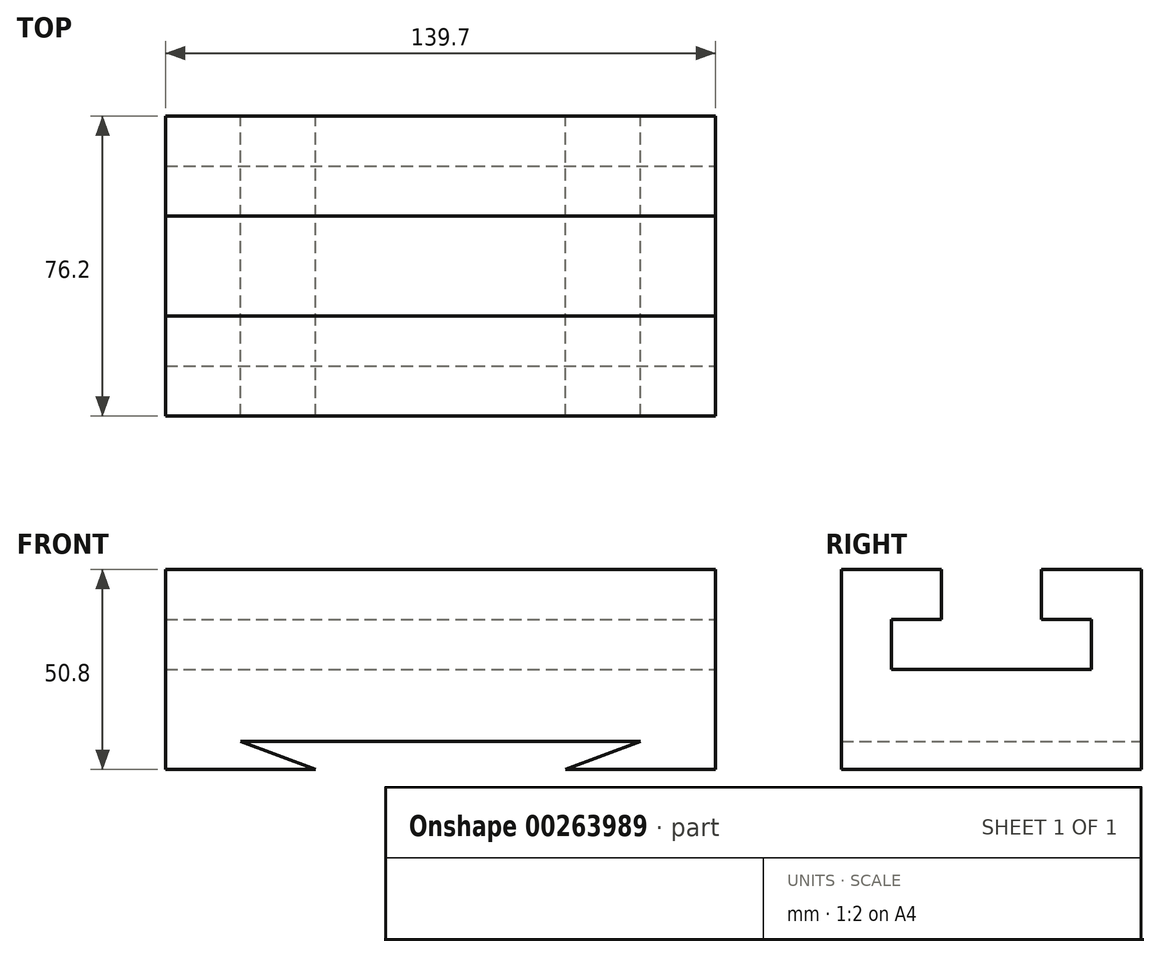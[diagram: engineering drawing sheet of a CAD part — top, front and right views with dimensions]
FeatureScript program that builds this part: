
annotation { "Feature Type Name" : "Feature", "Feature Type Description" : "" }
export const myFeature = defineFeature(function(context is Context, id is Id, definition is map)
    precondition{}
    {
        {
            var Q0;
            Q0=qCreatedBy(makeId("Front.planeOp"),FACE);
            var sketch = newSketch(context, id + "F0", { "sketchPlane" : qUnion([Q0])});
            skLineSegment(sketch, "E0", {"start": v(-77.12, 0) * mm, "end": v(-39.02, 0) * mm});
            skLineSegment(sketch, "E1", {"start": v(-39.02, 0) * mm, "end": v(-58.07, 7.07) * mm});
            skPoint(sketch, "E1.endSnap0", {"position": v(-58.07, 0) * mm});
            skLineSegment(sketch, "E2", {"start": v(-58.07, 7.07) * mm, "end": v(43.53, 7.07) * mm});
            skLineSegment(sketch, "E3", {"start": v(43.53, 7.07) * mm, "end": v(24.48, 0) * mm});
            skLineSegment(sketch, "E4", {"start": v(24.48, 0) * mm, "end": v(62.58, 0) * mm});
            skLineSegment(sketch, "E5", {"start": v(62.58, 0) * mm, "end": v(62.58, 50.8) * mm});
            skLineSegment(sketch, "E6", {"start": v(-77.12, 0) * mm, "end": v(-77.12, 50.8) * mm});
            skLineSegment(sketch, "E7", {"start": v(-77.12, 50.8) * mm, "end": v(62.58, 50.8) * mm});
            skSolve(sketch);
        }
        {
            var Q0;
            Q0 = qSketchRegion(id + "F0", true);
            extrude(context, id + "F1", {"entities" : qUnion([Q0]), "depth" : 76.2 * mm});
        }
        {
            var Q0;
            Q0=makeQuery(id+"F1.opExtrude","SWEPT_FACE",FACE,{"disambiguationData":[OSD([sQuery(id+"F0.wireOp",EDGE,"E5")])]});
            var sketch = newSketch(context, id + "F2", { "sketchPlane" : qUnion([Q0])});
            skLineSegment(sketch, "E8", {"start": v(-76.2, 50.8) * mm, "end": v(-50.8, 50.8) * mm});
            skLineSegment(sketch, "E9", {"start": v(-50.8, 50.8) * mm, "end": v(-50.8, 38.1) * mm});
            skLineSegment(sketch, "E10", {"start": v(-50.8, 38.1) * mm, "end": v(-63.5, 38.1) * mm});
            skLineSegment(sketch, "E11", {"start": v(-63.5, 38.1) * mm, "end": v(-63.5, 25.4) * mm});
            skLineSegment(sketch, "E12", {"start": v(-63.5, 25.4) * mm, "end": v(-12.7, 25.4) * mm});
            skLineSegment(sketch, "E13", {"start": v(-12.7, 25.4) * mm, "end": v(-12.7, 38.1) * mm});
            skLineSegment(sketch, "E14", {"start": v(-12.7, 38.1) * mm, "end": v(-25.4, 38.1) * mm});
            skLineSegment(sketch, "E15", {"start": v(-25.4, 38.1) * mm, "end": v(-25.4, 50.8) * mm});
            skLineSegment(sketch, "E16", {"start": v(-25.4, 50.8) * mm, "end": v(-50.8, 50.8) * mm});
            skSolve(sketch);
        }
        {
            var Q0;
            Q0=makeQuery(id+"F2.imprint","IMPRINT",FACE,{"disambiguationData":[TD([[makeQuery(id+"F2.imprint","IMPRINT",EDGE,{"derivedFrom":sQuery(id+"F2.wireOp",EDGE,"E9")}),1.0]])]});
            extrude(context, id + "F3", {"entities" : qUnion([Q0]), "operationType" : NewBodyOperationType.REMOVE, "endBound" : BoundingType.UP_TO_NEXT, "oppositeDirection" : true, "depth" : 89.66 * mm});
        }
    });
